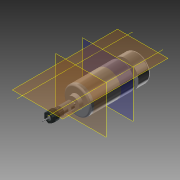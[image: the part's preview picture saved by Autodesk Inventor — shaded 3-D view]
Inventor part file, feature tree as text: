
AUTODESK INVENTOR PART (.ipt)
format: ipt  version: 2013 (Build 170138000, 138)  size: 303,104 bytes
history: native  units: mm
features: extrude x16, sketch x16, other x13, fillet x3, chamfer x2, projected_geometry x1
ambient origin geometry x8: Origin, YZ Plane, XZ Plane, XY Plane, X Axis, Y Axis, Z Axis, Center Point
feature tree (51):
  other  "Těleso1"
  extrude  "Vysunutí1"  Depth=26.0mm
  extrude  "Vysunutí2"  Depth=90.0mm TaperAngle=0.0deg
  fillet  "Zaoblení1"  Radius=13.0mm
  fillet  "Zaoblení2"  Radius=7.0mm
  extrude  "Vysunutí3"  Depth=3.0mm
  chamfer  "Zkosení1"  Distance=3.0mm
  extrude  "Vysunutí4"  Depth=4.0mm
  extrude  "Vysunutí5"  Depth=5.0mm TaperAngle=0.0deg
  extrude  "Vysunutí6"  Depth=7.0mm
  extrude  "Vysunutí7"  Depth=8.0mm
  extrude  "Vysunutí8"  Depth=44.0mm TaperAngle=0.0deg
  extrude  "Vysunutí9"  Depth=9.5mm
  chamfer  "Zkosení2"  Distance=13.0mm
  other  "Pracovní rovina1"
  extrude  "Vysunutí10"  Depth=5.0mm
  other  "Závit1"
  extrude  "Vysunutí11"  Depth=3.0mm TaperAngle=0.0deg
  extrude  "Vysunutí12"  Depth=5.0mm TaperAngle=0.0deg
  fillet  "Zaoblení3"  Radius=3.175mm
  extrude  "Vysunutí13"  Depth=5.0mm TaperAngle=0.0deg
  other  "Pracovní rovina2"
  extrude  "Vysunutí14"  Depth=2.0mm
  other  "Pracovní rovina5"
  other  "Pracovní rovina4"
  extrude  "Vysunutí15"  Depth=10.0mm TaperAngle=0.0deg
  other  "Pracovní rovina6"
  extrude  "Vysunutí16"  Depth=0.52mm
  other  "Pracovní rovina7"
  sketch  "Náčrt2"
  sketch  "Náčrt3"
  sketch  "Náčrt4"
  sketch  "Náčrt5"
  sketch  "Náčrt6"
  sketch  "Náčrt7"
  sketch  "Náčrt8"
  sketch  "Náčrt9"
  sketch  "Náčrt10"
  sketch  "Náčrt11"
  sketch  "Náčrt12"
  sketch  "Náčrt13"
  sketch  "Náčrt14"
  sketch  "Náčrt15"
  other  "Těleso2"
  sketch  "Náčrt17"
  other  "Těleso3"
  sketch  "Náčrt18"
  projected_geometry  "Promítnutá smyčka1"
  other  "Těleso4"
  other  "Pracovní osa1"
  other  "Pracovní osa2"
